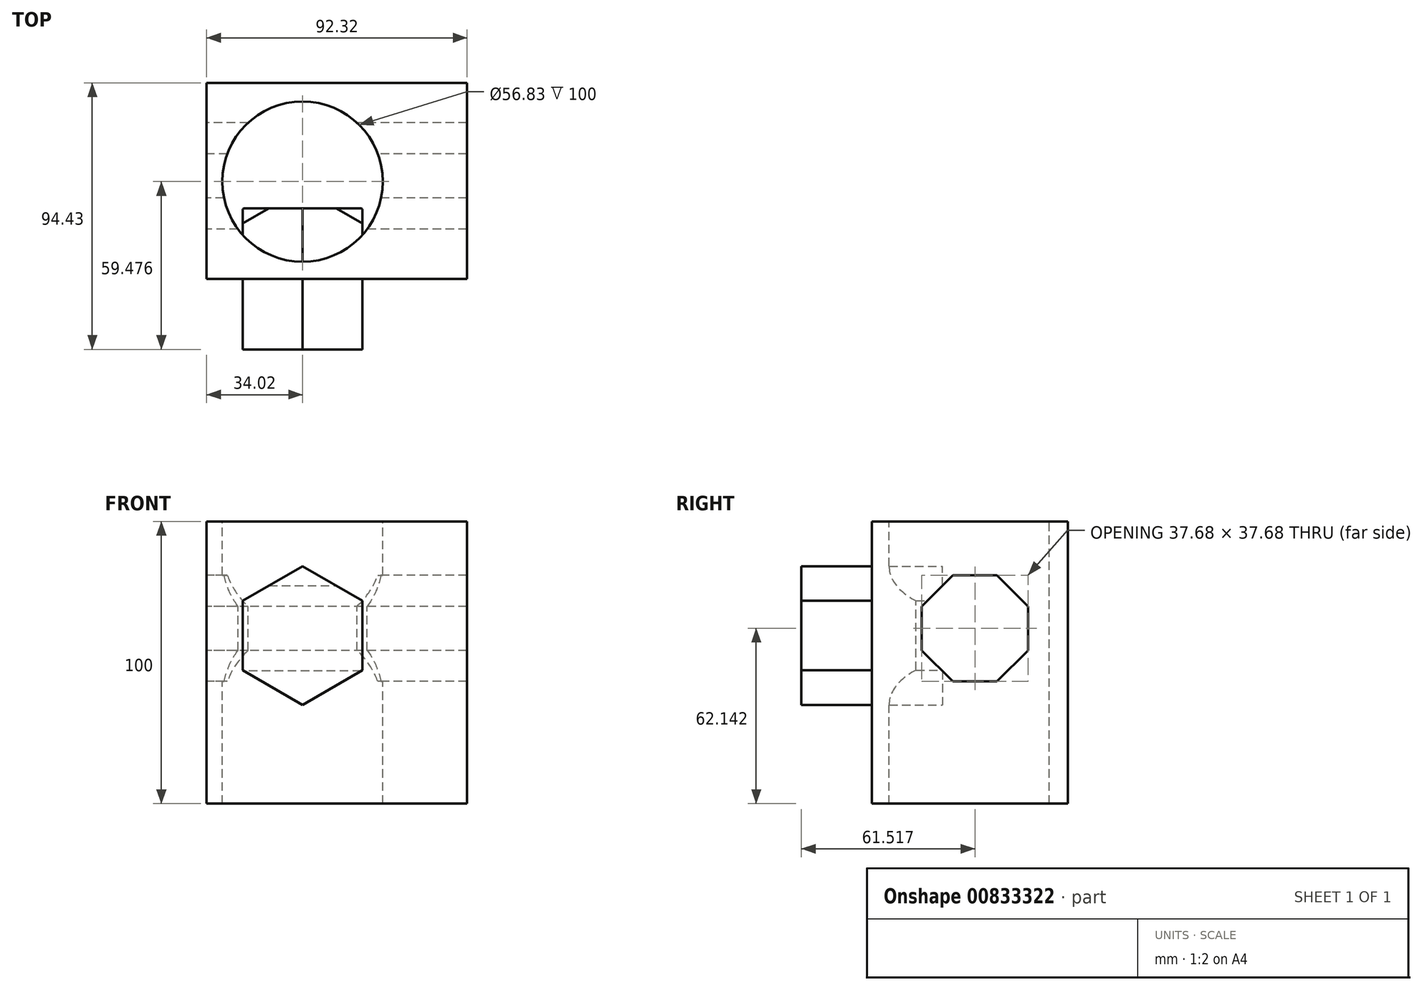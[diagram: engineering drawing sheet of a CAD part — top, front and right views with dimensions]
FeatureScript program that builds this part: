
annotation { "Feature Type Name" : "Feature", "Feature Type Description" : "" }
export const myFeature = defineFeature(function(context is Context, id is Id, definition is map)
    precondition{}
    {
        {
            var Q0;
            Q0=qCreatedBy(makeId("Top.planeOp"),FACE);
            var sketch = newSketch(context, id + "F0", { "sketchPlane" : qUnion([Q0])});
            skLineSegment(sketch, "E0.bottom", {"start": v(-34.02, 30.69) * mm, "end": v(33.3, 30.69) * mm});
            skLineSegment(sketch, "E0.top", {"start": v(-34.02, -38.74) * mm, "end": v(33.3, -38.74) * mm});
            skLineSegment(sketch, "E0.left", {"start": v(-34.02, 30.69) * mm, "end": v(-34.02, -38.74) * mm});
            skLineSegment(sketch, "E0.right", {"start": v(33.3, 30.69) * mm, "end": v(33.3, -38.74) * mm});
            skSolve(sketch);
        }
        {
            var Q0;
            Q0=makeQuery(id+"F0.imprint","IMPRINT",FACE,{"disambiguationData":[TD([[makeQuery(id+"F0.imprint","IMPRINT",EDGE,{"derivedFrom":sQuery(id+"F0.wireOp",EDGE,"E0.bottom")}),-1.0]])]});
            extrude(context, id + "F1", {"entities" : qUnion([Q0]), "depth" : 100 * mm, "offsetDistance" : 25 * mm});
        }
        {
            var Q0;
            Q0=makeQuery(id+"F1.opExtrude","CAP_FACE",FACE,{"disambiguationData":[OSD([sQuery(id+"F0.wireOp",EDGE,"E0.bottom"),sQuery(id+"F0.wireOp",EDGE,"E0.top"),sQuery(id+"F0.wireOp",EDGE,"E0.left"),sQuery(id+"F0.wireOp",EDGE,"E0.right")])],"isStart":false});
            var sketch = newSketch(context, id + "F2", { "sketchPlane" : qUnion([Q0])});
            skCircle(sketch, "E1", {"center": v(0, -4.26) * mm, "radius": 28.41 * mm});
            skSolve(sketch);
        }
        {
            var Q0;
            Q0=makeQuery(id+"F2.imprint","IMPRINT",FACE,{"disambiguationData":[TD([[makeQuery(id+"F2.imprint","IMPRINT",EDGE,{"derivedFrom":sQuery(id+"F2.wireOp",EDGE,"E1")}),1.0]])]});
            extrude(context, id + "F3", {"entities" : qUnion([Q0]), "operationType" : NewBodyOperationType.REMOVE, "endBound" : BoundingType.THROUGH_ALL, "oppositeDirection" : true, "depth" : 25 * mm, "offsetDistance" : 25 * mm});
        }
        {
            var Q0;
            Q0=makeQuery(id+"F1.opExtrude","SWEPT_FACE",FACE,{"disambiguationData":[OSD([sQuery(id+"F0.wireOp",EDGE,"E0.top")])]});
            var sketch = newSketch(context, id + "F4", { "sketchPlane" : qUnion([Q0])});
            skCircle(sketch, "E2.cCircle", {"center": v(0, 59.6) * mm, "radius": 21.28 * mm, "construction": true});
            skLineSegment(sketch, "E2.0", {"start": v(-21.28, 47.32) * mm, "end": v(-21.28, 71.89) * mm});
            skLineSegment(sketch, "E2.1", {"start": v(-21.28, 71.89) * mm, "end": v(0, 84.17) * mm});
            skLineSegment(sketch, "E2.2", {"start": v(0, 84.17) * mm, "end": v(21.28, 71.89) * mm});
            skLineSegment(sketch, "E2.3", {"start": v(21.28, 71.89) * mm, "end": v(21.28, 47.32) * mm});
            skLineSegment(sketch, "E2.4", {"start": v(21.28, 47.32) * mm, "end": v(0, 35.04) * mm});
            skLineSegment(sketch, "E2.5", {"start": v(0, 35.04) * mm, "end": v(-21.28, 47.32) * mm});
            skPoint(sketch, "E2.0.midPoint", {"position": v(-21.28, 59.6) * mm});
            skSolve(sketch);
        }
        {
            var Q0;
            Q0=makeQuery(id+"F4.imprint","IMPRINT",FACE,{"disambiguationData":[TD([[makeQuery(id+"F4.imprint","IMPRINT",EDGE,{"derivedFrom":sQuery(id+"F4.wireOp",EDGE,"E2.0")}),-1.0]])]});
            var Q1;
            Q1 = qSketchRegion(id + "F4", true);
            extrude(context, id + "F5", {"entities" : qUnion([Q0, Q1]), "operationType" : NewBodyOperationType.ADD, "depth" : 25 * mm, "offsetDistance" : 25 * mm, "hasSecondDirection" : true, "secondDirectionOppositeDirection" : true, "secondDirectionDepth" : 25 * mm});
        }
        {
            var Q0;
            Q0=makeQuery(id+"F1.opExtrude","SWEPT_FACE",FACE,{"disambiguationData":[OSD([sQuery(id+"F0.wireOp",EDGE,"E0.right")])]});
            extrude(context, id + "F6", {"entities" : qUnion([Q0]), "operationType" : NewBodyOperationType.ADD, "depth" : 25 * mm, "offsetDistance" : 25 * mm});
        }
        {
            var Q0;
            Q0=makeQuery(id+"F1.opExtrude","SWEPT_FACE",FACE,{"disambiguationData":[OSD([sQuery(id+"F0.wireOp",EDGE,"E0.left")])]});
            var sketch = newSketch(context, id + "F7", { "sketchPlane" : qUnion([Q0])});
            skCircle(sketch, "E3.cCircle", {"center": v(2.22, 62.14) * mm, "radius": 18.84 * mm, "construction": true});
            skLineSegment(sketch, "E3.0", {"start": v(21.06, 69.95) * mm, "end": v(21.06, 54.34) * mm});
            skLineSegment(sketch, "E3.1", {"start": v(21.06, 54.34) * mm, "end": v(10.03, 43.3) * mm});
            skLineSegment(sketch, "E3.2", {"start": v(10.03, 43.3) * mm, "end": v(-5.58, 43.3) * mm});
            skLineSegment(sketch, "E3.3", {"start": v(-5.58, 43.3) * mm, "end": v(-16.62, 54.34) * mm});
            skLineSegment(sketch, "E3.4", {"start": v(-16.62, 54.34) * mm, "end": v(-16.62, 69.95) * mm});
            skLineSegment(sketch, "E3.5", {"start": v(-16.62, 69.95) * mm, "end": v(-5.58, 80.98) * mm});
            skLineSegment(sketch, "E3.6", {"start": v(-5.58, 80.98) * mm, "end": v(10.03, 80.98) * mm});
            skLineSegment(sketch, "E3.7", {"start": v(10.03, 80.98) * mm, "end": v(21.06, 69.95) * mm});
            skPoint(sketch, "E3.0.midPoint", {"position": v(21.06, 62.14) * mm});
            skSolve(sketch);
        }
        {
            var Q0;
            Q0=makeQuery(id+"F7.imprint","IMPRINT",FACE,{"disambiguationData":[TD([[makeQuery(id+"F7.imprint","IMPRINT",EDGE,{"derivedFrom":sQuery(id+"F7.wireOp",EDGE,"E3.0")}),-1.0]])]});
            extrude(context, id + "F8", {"entities" : qUnion([Q0]), "operationType" : NewBodyOperationType.REMOVE, "endBound" : BoundingType.THROUGH_ALL, "oppositeDirection" : true, "depth" : 25 * mm, "offsetDistance" : 25 * mm});
        }
    });
